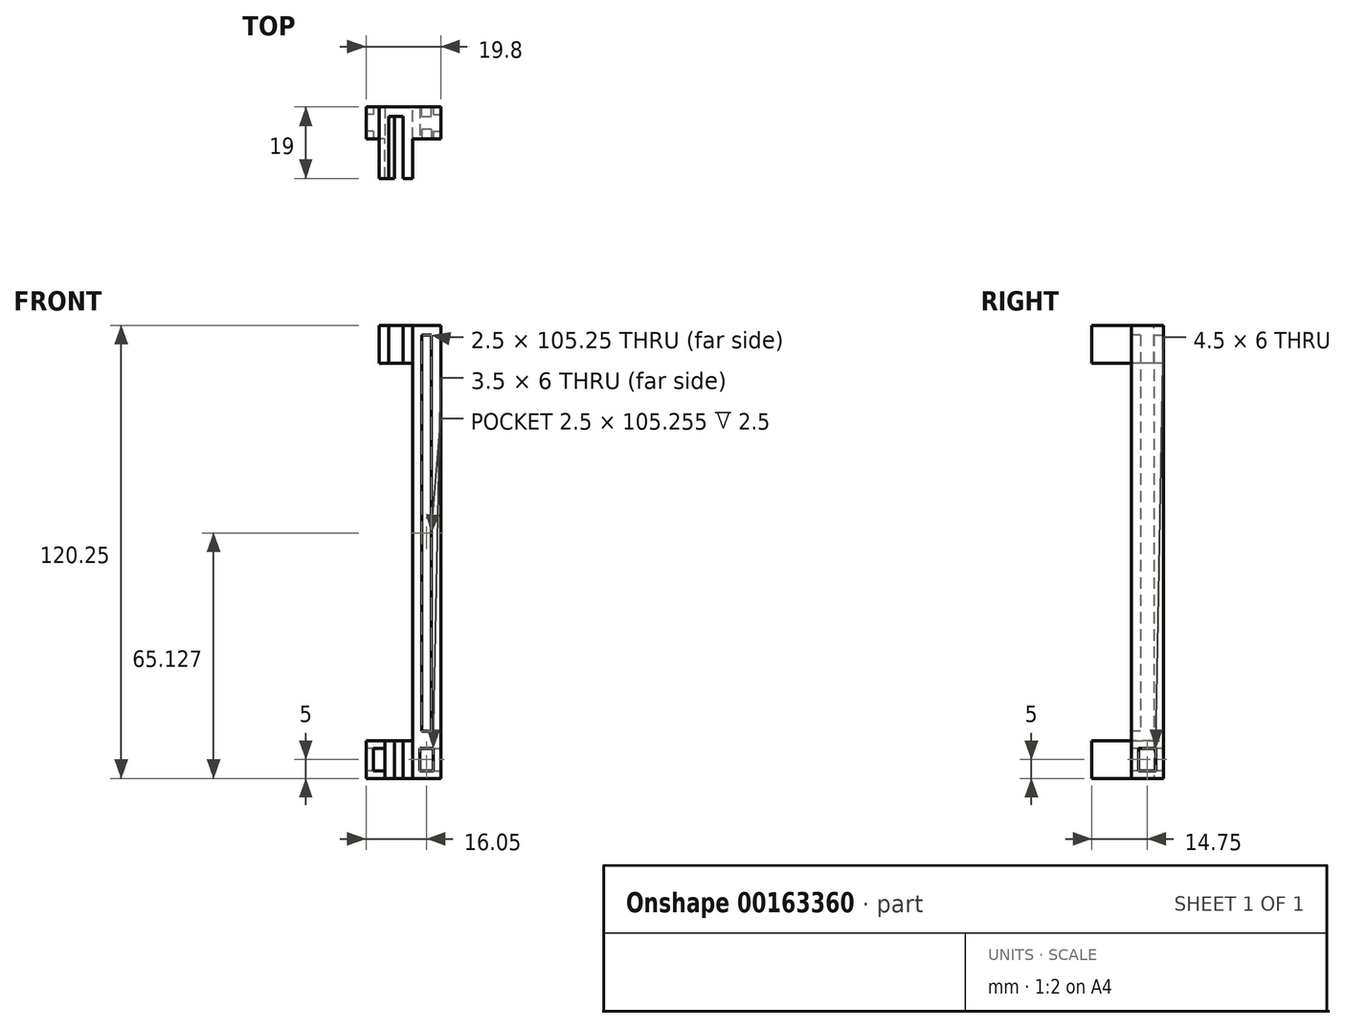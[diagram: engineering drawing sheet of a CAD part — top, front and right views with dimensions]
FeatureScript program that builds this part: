
annotation { "Feature Type Name" : "Feature", "Feature Type Description" : "" }
export const myFeature = defineFeature(function(context is Context, id is Id, definition is map)
    precondition{}
    {
        {
            var Q0;
            Q0=qCreatedBy(makeId("Top.planeOp"),FACE);
            var sketch = newSketch(context, id + "F0", { "sketchPlane" : qUnion([Q0])});
            skLineSegment(sketch, "E0", {"start": v(0, 0) * mm, "end": v(0, -8.5) * mm});
            skLineSegment(sketch, "E1", {"start": v(0, -8.5) * mm, "end": v(-7.5, -8.5) * mm});
            skLineSegment(sketch, "E2", {"start": v(-10, -2.5) * mm, "end": v(-12.3, -2.5) * mm});
            skLineSegment(sketch, "E3", {"start": v(-14.8, -8.5) * mm, "end": v(-19.8, -8.5) * mm});
            skLineSegment(sketch, "E4", {"start": v(-19.8, -8.5) * mm, "end": v(-19.8, 0) * mm});
            skLineSegment(sketch, "E5", {"start": v(-19.8, 0) * mm, "end": v(0, 0) * mm});
            skLineSegment(sketch, "E6", {"start": v(-7.5, -8.5) * mm, "end": v(-7.5, -19) * mm});
            skLineSegment(sketch, "E7", {"start": v(-7.5, -19) * mm, "end": v(-10, -19) * mm});
            skLineSegment(sketch, "E8", {"start": v(-10, -19) * mm, "end": v(-10, -2.5) * mm});
            skLineSegment(sketch, "E9", {"start": v(-12.3, -2.5) * mm, "end": v(-12.3, -19) * mm});
            skLineSegment(sketch, "E10", {"start": v(-12.3, -19) * mm, "end": v(-14.8, -19) * mm});
            skLineSegment(sketch, "E11", {"start": v(-14.8, -19) * mm, "end": v(-14.8, -8.5) * mm});
            skLineSegment(sketch, "E12", {"start": v(-11.15, -2.5) * mm, "end": v(-11.15, 0) * mm, "construction": true});
            skSolve(sketch);
        }
        {
            var Q0;
            Q0 = qSketchRegion(id + "F0", true);
            extrude(context, id + "F1", {"entities" : qUnion([Q0]), "depth" : 10 * mm});
        }
        {
            var Q0;
            Q0=makeQuery(id+"F1.opExtrude","CAP_FACE",FACE,{"disambiguationData":[OSD([sQuery(id+"F0.wireOp",EDGE,"E0"),sQuery(id+"F0.wireOp",EDGE,"E1"),sQuery(id+"F0.wireOp",EDGE,"E2"),sQuery(id+"F0.wireOp",EDGE,"E3"),sQuery(id+"F0.wireOp",EDGE,"E4"),sQuery(id+"F0.wireOp",EDGE,"E5"),sQuery(id+"F0.wireOp",EDGE,"E6"),sQuery(id+"F0.wireOp",EDGE,"E7"),sQuery(id+"F0.wireOp",EDGE,"E8"),sQuery(id+"F0.wireOp",EDGE,"E9"),sQuery(id+"F0.wireOp",EDGE,"E10"),sQuery(id+"F0.wireOp",EDGE,"E11")])],"isStart":false});
            var sketch = newSketch(context, id + "F2", { "sketchPlane" : qUnion([Q0])});
            skLineSegment(sketch, "E13.bottom", {"start": v(0, -8.5) * mm, "end": v(-7.5, -8.5) * mm});
            skLineSegment(sketch, "E13.top", {"start": v(0, 0) * mm, "end": v(-7.5, 0) * mm});
            skLineSegment(sketch, "E13.left", {"start": v(0, -8.5) * mm, "end": v(0, 0) * mm});
            skLineSegment(sketch, "E13.right", {"start": v(-7.5, -8.5) * mm, "end": v(-7.5, 0) * mm});
            skSolve(sketch);
        }
        {
            var Q0;
            Q0 = qSketchRegion(id + "F2", true);
            extrude(context, id + "F3", {"entities" : qUnion([Q0]), "operationType" : NewBodyOperationType.ADD, "depth" : 110.25 * mm});
        }
        {
            var Q0;
            Q0=makeQuery(id+"F3.opExtrude","CAP_FACE",FACE,{"disambiguationData":[OSD([sQuery(id+"F2.wireOp",EDGE,"E13.bottom"),sQuery(id+"F2.wireOp",EDGE,"E13.top"),sQuery(id+"F2.wireOp",EDGE,"E13.left"),sQuery(id+"F2.wireOp",EDGE,"E13.right")])],"isStart":false});
            var sketch = newSketch(context, id + "F4", { "sketchPlane" : qUnion([Q0])});
            skLineSegment(sketch, "E14", {"start": v(-7.5, 0) * mm, "end": v(-7.5, -19) * mm});
            skLineSegment(sketch, "E15", {"start": v(-7.5, -19) * mm, "end": v(-10, -19) * mm});
            skLineSegment(sketch, "E16", {"start": v(-10, -19) * mm, "end": v(-10, -2.5) * mm});
            skLineSegment(sketch, "E17", {"start": v(-10, -2.5) * mm, "end": v(-13.8, -2.5) * mm});
            skLineSegment(sketch, "E18", {"start": v(-13.8, -2.5) * mm, "end": v(-13.8, -19) * mm});
            skLineSegment(sketch, "E19", {"start": v(-13.8, -19) * mm, "end": v(-16.3, -19) * mm});
            skLineSegment(sketch, "E20", {"start": v(-16.3, -19) * mm, "end": v(-16.3, 0) * mm});
            skLineSegment(sketch, "E21", {"start": v(-16.3, 0) * mm, "end": v(-7.5, 0) * mm});
            skLineSegment(sketch, "E22", {"start": v(-11.9, 0) * mm, "end": v(-11.9, -2.5) * mm, "construction": true});
            skSolve(sketch);
        }
        {
            var Q0;
            Q0 = qSketchRegion(id + "F4", true);
            extrude(context, id + "F5", {"entities" : qUnion([Q0]), "operationType" : NewBodyOperationType.ADD, "oppositeDirection" : true, "depth" : 10 * mm});
        }
        {
            var Q0;
            Q0=makeQuery(id+"F1.opExtrude","SWEPT_FACE",FACE,{"disambiguationData":[OSD([sQuery(id+"F0.wireOp",EDGE,"E4")])]});
            var sketch = newSketch(context, id + "F6", { "sketchPlane" : qUnion([Q0])});
            skLineSegment(sketch, "E23.0", {"start": v(2, 2) * mm, "end": v(6.5, 2) * mm});
            skLineSegment(sketch, "E23.1", {"start": v(2, 8) * mm, "end": v(2, 2) * mm});
            skLineSegment(sketch, "E23.2", {"start": v(6.5, 8) * mm, "end": v(2, 8) * mm});
            skLineSegment(sketch, "E23.3", {"start": v(6.5, 2) * mm, "end": v(6.5, 8) * mm});
            skSolve(sketch);
        }
        {
            var Q0;
            Q0 = qSketchRegion(id + "F6", true);
            var Q1;
            Q1=makeQuery(id+"F1.opExtrude","SWEPT_FACE",FACE,{"disambiguationData":[OSD([sQuery(id+"F0.wireOp",EDGE,"E11")])]});
            extrude(context, id + "F7", {"entities" : qUnion([Q0]), "operationType" : NewBodyOperationType.REMOVE, "endBound" : BoundingType.UP_TO_SURFACE, "oppositeDirection" : true, "endBoundEntityFace" : qUnion([Q1]), "depth" : 25 * mm});
        }
        {
            var Q0;
            Q0=makeQuery(id+"F1.opExtrude","SWEPT_FACE",FACE,{"disambiguationData":[OSD([sQuery(id+"F0.wireOp",EDGE,"E3")])]});
            var sketch = newSketch(context, id + "F8", { "sketchPlane" : qUnion([Q0])});
            skLineSegment(sketch, "E24.0", {"start": v(-14.8, 10) * mm, "end": v(-14.8, 0) * mm});
            skLineSegment(sketch, "E25", {"start": v(-14.8, 8) * mm, "end": v(-17.8, 8) * mm});
            skLineSegment(sketch, "E26", {"start": v(-17.8, 8) * mm, "end": v(-17.8, 2) * mm});
            skLineSegment(sketch, "E27", {"start": v(-17.8, 2) * mm, "end": v(-14.8, 2) * mm});
            skLineSegment(sketch, "E28.0", {"start": v(-19.8, 10) * mm, "end": v(-19.8, 0) * mm, "construction": true});
            skLineSegment(sketch, "E28.1", {"start": v(-14.8, 10) * mm, "end": v(-19.8, 10) * mm, "construction": true});
            skLineSegment(sketch, "E28.2", {"start": v(-14.8, 0) * mm, "end": v(-19.8, 0) * mm, "construction": true});
            skLineSegment(sketch, "E29", {"start": v(-19.8, 5) * mm, "end": v(-17.8, 5) * mm, "construction": true});
            skLineSegment(sketch, "E30", {"start": v(-17.3, 10) * mm, "end": v(-17.3, 8) * mm, "construction": true});
            skLineSegment(sketch, "E31", {"start": v(-17.3, 0) * mm, "end": v(-17.3, 2) * mm, "construction": true});
            skSolve(sketch);
        }
        {
            var Q0;
            Q0 = qSketchRegion(id + "F8", true);
            extrude(context, id + "F9", {"entities" : qUnion([Q0]), "operationType" : NewBodyOperationType.REMOVE, "endBound" : BoundingType.THROUGH_ALL, "oppositeDirection" : true, "depth" : 25 * mm});
        }
        {
            var Q0;
            Q0=makeQuery(id+"F3.boolean.opBoolean","MERGE",FACE,{"derivedFrom":[makeQuery(id+"F1.opExtrude","SWEPT_FACE",FACE,{"disambiguationData":[OSD([sQuery(id+"F0.wireOp",EDGE,"E0")])]}),makeQuery(id+"F3.opExtrude","SWEPT_FACE",FACE,{"disambiguationData":[OSD([sQuery(id+"F2.wireOp",EDGE,"E13.left")])]})]});
            var sketch = newSketch(context, id + "F10", { "sketchPlane" : qUnion([Q0])});
            skLineSegment(sketch, "E32.0", {"start": v(-8.5, 10) * mm, "end": v(-19, 10) * mm, "construction": true});
            skLineSegment(sketch, "E33", {"start": v(-8.5, 10) * mm, "end": v(0, 10) * mm, "construction": true});
            skLineSegment(sketch, "E34", {"start": v(-8.5, 10) * mm, "end": v(-8.5, 0) * mm, "construction": true});
            skLineSegment(sketch, "E35", {"start": v(-8.5, 0) * mm, "end": v(0, 0) * mm, "construction": true});
            skLineSegment(sketch, "E36", {"start": v(0, 0) * mm, "end": v(0, 10) * mm, "construction": true});
            skLineSegment(sketch, "E37.0", {"start": v(-6.5, 8) * mm, "end": v(-2, 8) * mm});
            skLineSegment(sketch, "E37.1", {"start": v(-6.5, 8) * mm, "end": v(-6.5, 2) * mm});
            skLineSegment(sketch, "E37.2", {"start": v(-6.5, 2) * mm, "end": v(-2, 2) * mm});
            skLineSegment(sketch, "E37.3", {"start": v(-2, 2) * mm, "end": v(-2, 8) * mm});
            skSolve(sketch);
        }
        {
            var Q0;
            Q0 = qSketchRegion(id + "F10", true);
            extrude(context, id + "F11", {"entities" : qUnion([Q0]), "operationType" : NewBodyOperationType.REMOVE, "oppositeDirection" : true, "depth" : 5 * mm});
        }
        {
            var Q0;
            Q0=makeQuery(id+"F3.boolean.opBoolean","MERGE",FACE,{"derivedFrom":[makeQuery(id+"F1.opExtrude","SWEPT_FACE",FACE,{"disambiguationData":[OSD([sQuery(id+"F0.wireOp",EDGE,"E1")])]}),makeQuery(id+"F3.opExtrude","SWEPT_FACE",FACE,{"disambiguationData":[OSD([sQuery(id+"F2.wireOp",EDGE,"E13.bottom")])]})]});
            var sketch = newSketch(context, id + "F12", { "sketchPlane" : qUnion([Q0])});
            skLineSegment(sketch, "E38", {"start": v(-7.5, 10) * mm, "end": v(0, 10) * mm, "construction": true});
            skLineSegment(sketch, "E39", {"start": v(0, 10) * mm, "end": v(0, 0) * mm, "construction": true});
            skLineSegment(sketch, "E40", {"start": v(0, 0) * mm, "end": v(-7.5, 0) * mm, "construction": true});
            skLineSegment(sketch, "E41", {"start": v(-7.5, 0) * mm, "end": v(-7.5, 10) * mm, "construction": true});
            skLineSegment(sketch, "E42.0", {"start": v(-2, 8) * mm, "end": v(-2, 2) * mm});
            skLineSegment(sketch, "E42.1", {"start": v(-5.5, 8) * mm, "end": v(-2, 8) * mm});
            skLineSegment(sketch, "E42.2", {"start": v(-5.5, 2) * mm, "end": v(-5.5, 8) * mm});
            skLineSegment(sketch, "E42.3", {"start": v(-2, 2) * mm, "end": v(-5.5, 2) * mm});
            skSolve(sketch);
        }
        {
            var Q0;
            Q0 = qSketchRegion(id + "F12", true);
            extrude(context, id + "F13", {"entities" : qUnion([Q0]), "operationType" : NewBodyOperationType.REMOVE, "endBound" : BoundingType.THROUGH_ALL, "oppositeDirection" : true, "depth" : 25 * mm});
        }
        {
            var Q0;
            Q0=makeQuery(id+"F5.boolean.opBoolean","MERGE",FACE,{"derivedFrom":[makeQuery(id+"F3.boolean.opBoolean","MERGE",FACE,{"derivedFrom":[makeQuery(id+"F1.opExtrude","SWEPT_FACE",FACE,{"disambiguationData":[OSD([sQuery(id+"F0.wireOp",EDGE,"E5")])]}),makeQuery(id+"F3.opExtrude","SWEPT_FACE",FACE,{"disambiguationData":[OSD([sQuery(id+"F2.wireOp",EDGE,"E13.top")])]})]}),makeQuery(id+"F5.opExtrude","SWEPT_FACE",FACE,{"disambiguationData":[OSD([sQuery(id+"F4.wireOp",EDGE,"E21")])]})]});
            var sketch = newSketch(context, id + "F14", { "sketchPlane" : qUnion([Q0])});
            skLineSegment(sketch, "E43", {"start": v(0, 120.25) * mm, "end": v(0, 10) * mm, "construction": true});
            skLineSegment(sketch, "E44", {"start": v(0, 10) * mm, "end": v(7.5, 10) * mm, "construction": true});
            skLineSegment(sketch, "E45", {"start": v(7.5, 10) * mm, "end": v(7.5, 120.25) * mm, "construction": true});
            skLineSegment(sketch, "E46", {"start": v(7.5, 120.25) * mm, "end": v(0, 120.25) * mm, "construction": true});
            skLineSegment(sketch, "E47.0", {"start": v(2.5, 117.75) * mm, "end": v(2.5, 12.5) * mm});
            skLineSegment(sketch, "E47.1", {"start": v(5, 117.75) * mm, "end": v(2.5, 117.75) * mm});
            skLineSegment(sketch, "E47.2", {"start": v(5, 12.5) * mm, "end": v(5, 117.75) * mm});
            skLineSegment(sketch, "E47.3", {"start": v(2.5, 12.5) * mm, "end": v(5, 12.5) * mm});
            skSolve(sketch);
        }
        {
            var Q0;
            Q0 = qSketchRegion(id + "F14", true);
            extrude(context, id + "F15", {"entities" : qUnion([Q0]), "operationType" : NewBodyOperationType.REMOVE, "oppositeDirection" : true, "depth" : 2.5 * mm});
        }
        {
            var Q0;
            Q0=makeQuery(id+"F3.boolean.opBoolean","MERGE",FACE,{"derivedFrom":[makeQuery(id+"F1.opExtrude","SWEPT_FACE",FACE,{"disambiguationData":[OSD([sQuery(id+"F0.wireOp",EDGE,"E1")])]}),makeQuery(id+"F3.opExtrude","SWEPT_FACE",FACE,{"disambiguationData":[OSD([sQuery(id+"F2.wireOp",EDGE,"E13.bottom")])]})]});
            var sketch = newSketch(context, id + "F16", { "sketchPlane" : qUnion([Q0])});
            skLineSegment(sketch, "E48", {"start": v(-7.5, 120.25) * mm, "end": v(-7.5, 10) * mm, "construction": true});
            skLineSegment(sketch, "E49", {"start": v(-7.5, 10) * mm, "end": v(0, 10) * mm, "construction": true});
            skLineSegment(sketch, "E50", {"start": v(0, 10) * mm, "end": v(0, 120.25) * mm, "construction": true});
            skLineSegment(sketch, "E51", {"start": v(0, 120.25) * mm, "end": v(-7.5, 120.25) * mm, "construction": true});
            skLineSegment(sketch, "E52.0", {"start": v(-5, 117.75) * mm, "end": v(-5, 12.5) * mm});
            skLineSegment(sketch, "E52.1", {"start": v(-2.5, 117.75) * mm, "end": v(-5, 117.75) * mm});
            skLineSegment(sketch, "E52.2", {"start": v(-2.5, 12.5) * mm, "end": v(-2.5, 117.75) * mm});
            skLineSegment(sketch, "E52.3", {"start": v(-5, 12.5) * mm, "end": v(-2.5, 12.5) * mm});
            skSolve(sketch);
        }
        {
            var Q0;
            Q0 = qSketchRegion(id + "F16", true);
            extrude(context, id + "F17", {"entities" : qUnion([Q0]), "operationType" : NewBodyOperationType.REMOVE, "oppositeDirection" : true, "depth" : 2.5 * mm});
        }
    });
